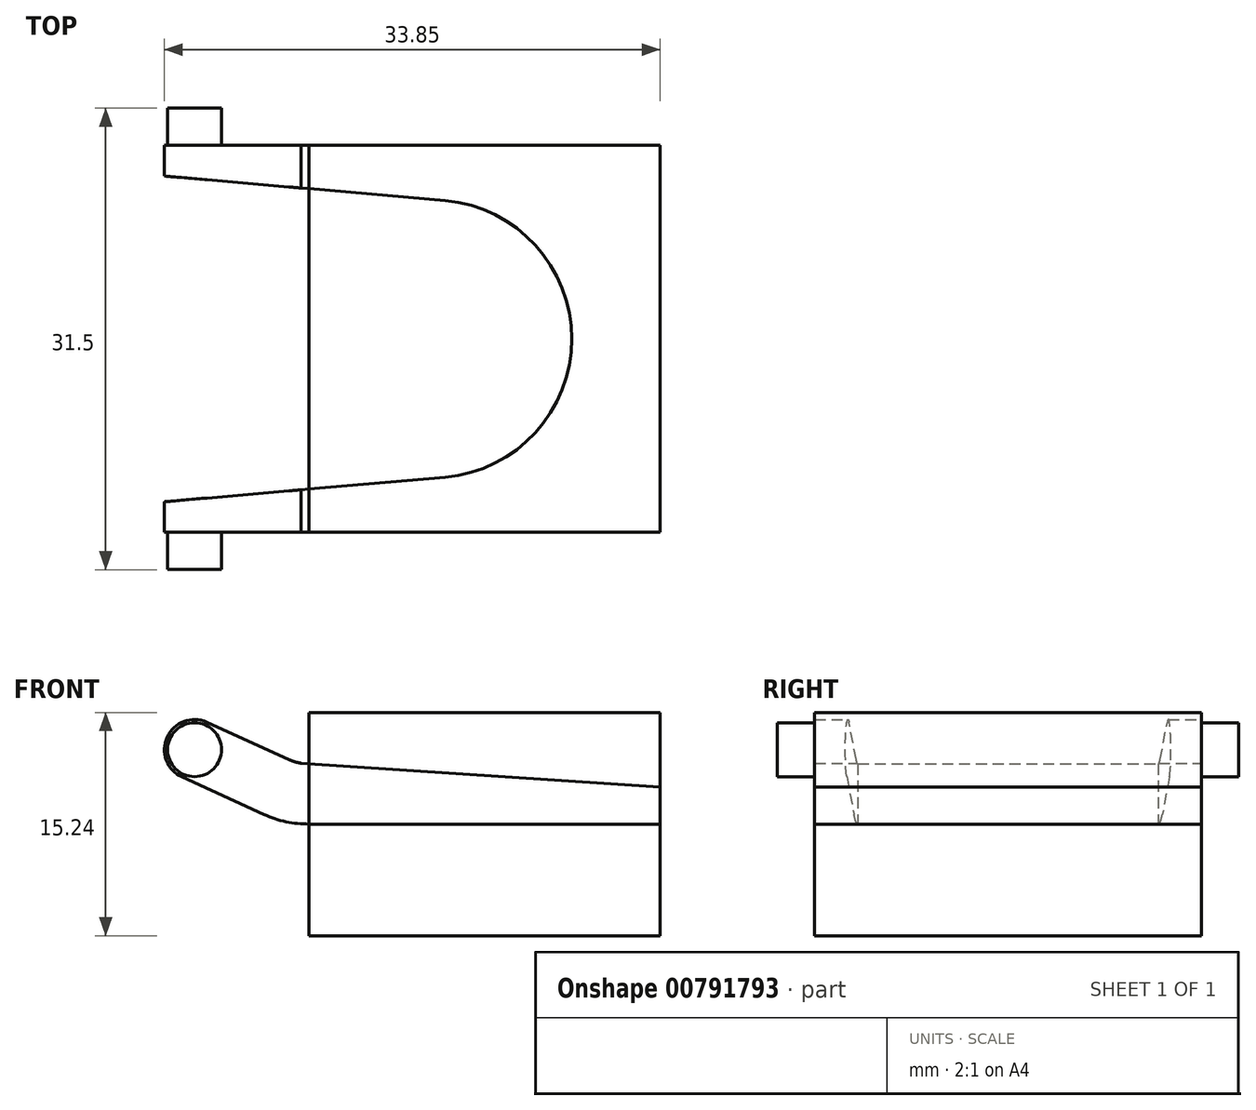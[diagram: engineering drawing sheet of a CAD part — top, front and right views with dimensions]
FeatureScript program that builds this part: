
annotation { "Feature Type Name" : "Feature", "Feature Type Description" : "" }
export const myFeature = defineFeature(function(context is Context, id is Id, definition is map)
    precondition{}
    {
        {
            var Q0;
            Q0=qCreatedBy(makeId("Front.planeOp"),FACE);
            var sketch = newSketch(context, id + "F0", { "sketchPlane" : qUnion([Q0])});
            skLineSegment(sketch, "E0", {"start": v(18.98, -6.5) * mm, "end": v(-4.99, -6.5) * mm});
            skLineSegment(sketch, "E1", {"start": v(-8.07, -5.85) * mm, "end": v(-13.66, -3.3) * mm});
            skLineSegment(sketch, "E2", {"start": v(18.98, -6.5) * mm, "end": v(18.98, -3.97) * mm});
            skLineSegment(sketch, "E3", {"start": v(18.98, -3.97) * mm, "end": v(-5.54, -2.36) * mm});
            skLineSegment(sketch, "E4", {"start": v(-11.96, 0.44) * mm, "end": v(-6.36, -2.1) * mm});
            skArc(sketch, "E5", {"start": v(-13.66, -3.3) * mm, "mid": v(-14.68, -0.57) * mm, "end": v(-11.96, 0.44) * mm});
            skLineSegment(sketch, "E6", {"start": v(-8.07, -5.85) * mm, "end": v(-6.36, -2.1) * mm, "construction": true});
            skArc(sketch, "E7", {"start": v(-8.07, -5.85) * mm, "mid": v(-6.57, -6.35) * mm, "end": v(-4.99, -6.5) * mm});
            skArc(sketch, "E8", {"start": v(-6.36, -2.1) * mm, "mid": v(-5.96, -2.26) * mm, "end": v(-5.54, -2.36) * mm});
            skSolve(sketch);
        }
        {
            var Q0;
            Q0=makeQuery(id+"F0.imprint","IMPRINT",FACE,{"disambiguationData":[TD([[makeQuery(id+"F0.imprint","IMPRINT",EDGE,{"derivedFrom":sQuery(id+"F0.wireOp",EDGE,"E0")}),-1.0]])]});
            extrude(context, id + "F1", {"entities" : qUnion([Q0]), "depth" : 26.42 * mm, "offsetDistance" : 25.4 * mm});
        }
        {
            var Q0;
            Q0=makeQuery(id+"F1.opExtrude","CAP_FACE",FACE,{"disambiguationData":[OSD([sQuery(id+"F0.wireOp",EDGE,"E0"),sQuery(id+"F0.wireOp",EDGE,"E1"),sQuery(id+"F0.wireOp",EDGE,"E2"),sQuery(id+"F0.wireOp",EDGE,"E3"),sQuery(id+"F0.wireOp",EDGE,"E4"),sQuery(id+"F0.wireOp",EDGE,"E5"),sQuery(id+"F0.wireOp",EDGE,"E7"),sQuery(id+"F0.wireOp",EDGE,"E8")])],"isStart":false});
            var sketch = newSketch(context, id + "F2", { "sketchPlane" : qUnion([Q0])});
            skArc(sketch, "E9.0", {"start": v(-13.66, -3.3) * mm, "mid": v(-14.68, -0.57) * mm, "end": v(-11.96, 0.44) * mm});
            skCircle(sketch, "E10", {"center": v(-12.8, -1.43) * mm, "radius": 1.84 * mm});
            skSolve(sketch);
        }
        {
            var Q0;
            Q0=makeQuery(id+"F2.imprint","IMPRINT",FACE,{"disambiguationData":[TD([[makeQuery(id+"F2.imprint","IMPRINT",EDGE,{"derivedFrom":sQuery(id+"F2.wireOp",EDGE,"E10")}),1.0]])]});
            extrude(context, id + "F3", {"entities" : qUnion([Q0]), "depth" : 2.54 * mm, "offsetDistance" : 25.4 * mm});
        }
        {
            var Q0;
            Q0=makeQuery(id+"F1.opExtrude","CAP_FACE",FACE,{"disambiguationData":[OSD([sQuery(id+"F0.wireOp",EDGE,"E0"),sQuery(id+"F0.wireOp",EDGE,"E1"),sQuery(id+"F0.wireOp",EDGE,"E2"),sQuery(id+"F0.wireOp",EDGE,"E3"),sQuery(id+"F0.wireOp",EDGE,"E4"),sQuery(id+"F0.wireOp",EDGE,"E5"),sQuery(id+"F0.wireOp",EDGE,"E7"),sQuery(id+"F0.wireOp",EDGE,"E8")])],"isStart":true});
            var Q1;
            Q1=makeQuery(id+"F1.opExtrude","CAP_FACE",FACE,{"disambiguationData":[OSD([sQuery(id+"F0.wireOp",EDGE,"E0"),sQuery(id+"F0.wireOp",EDGE,"E1"),sQuery(id+"F0.wireOp",EDGE,"E2"),sQuery(id+"F0.wireOp",EDGE,"E3"),sQuery(id+"F0.wireOp",EDGE,"E4"),sQuery(id+"F0.wireOp",EDGE,"E5"),sQuery(id+"F0.wireOp",EDGE,"E7"),sQuery(id+"F0.wireOp",EDGE,"E8")])],"isStart":false});
            cPlane(context, id + "F4", {"entities" : qUnion([Q0, Q1]), "cplaneType" : CPlaneType.MID_PLANE, "offset" : 25.4 * mm, "width" : 152.4 * mm, "height" : 152.4 * mm});
        }
        {
            var Q0;
            Q0=makeQuery(id+"F3.opExtrude","SWEPT_BODY",BODY,{"disambiguationData":[OSD([sQuery(id+"F2.wireOp",EDGE,"E10")])]});
            var Q1;
            Q1=qCreatedBy(id+"F4.planeOp",FACE);
            mirror(context, id + "F5", {"entities" : qUnion([Q0]), "mirrorPlane" : qUnion([Q1])});
        }
        {
            var Q0;
            Q0=makeQuery(id+"F1.opExtrude","SWEPT_FACE",FACE,{"disambiguationData":[OSD([sQuery(id+"F0.wireOp",EDGE,"E0")])]});
            var sketch = newSketch(context, id + "F6", { "sketchPlane" : qUnion([Q0])});
            skLineSegment(sketch, "E11", {"start": v(-16.56, 24.47) * mm, "end": v(-16.56, 1.94) * mm});
            skLineSegment(sketch, "E12", {"start": v(-16.56, 1.94) * mm, "end": v(4.29, 3.77) * mm});
            skLineSegment(sketch, "E13", {"start": v(-16.56, 24.47) * mm, "end": v(4.29, 22.65) * mm});
            skPoint(sketch, "E14", {"position": v(-16.56, 13.2) * mm});
            skPoint(sketch, "E15", {"position": v(-4.99, 13.2) * mm});
            skArc(sketch, "E16", {"start": v(4.29, 22.65) * mm, "mid": v(12.94, 13.2) * mm, "end": v(4.29, 3.77) * mm});
            skSolve(sketch);
        }
        {
            var Q0;
            {var subQ0=sQuery(id+"F6.wireOp",EDGE,"E11");Q0=makeQuery(id+"F6.imprint","IMPRINT",FACE,{"disambiguationData":[TD([[makeQuery(id+"F6.imprint","IMPRINT",EDGE,{"derivedFrom":subQ0}),1.0]])]});}
            var Q1;
            {var subQ0=sQuery(id+"F6.wireOp",EDGE,"E16");Q1=makeQuery(id+"F6.imprint","IMPRINT",FACE,{"disambiguationData":[TD([[makeQuery(id+"F6.imprint","IMPRINT",EDGE,{"derivedFrom":subQ0}),-1.0]])]});}
            extrude(context, id + "F7", {"entities" : qUnion([Q0, Q1]), "oppositeDirection" : true, "depth" : 15.24 * mm, "offsetDistance" : 25.4 * mm, "symmetric" : true});
        }
        {
            var Q0;
            Q0=makeQuery(id+"F7.opExtrude","SWEPT_BODY",BODY,{"disambiguationData":[OSD([sQuery(id+"F6.wireOp",EDGE,"E11"),sQuery(id+"F6.wireOp",EDGE,"E12"),sQuery(id+"F6.wireOp",EDGE,"E13"),sQuery(id+"F6.wireOp",EDGE,"E16")])]});
            var Q1;
            Q1=makeQuery(id+"F1.opExtrude","SWEPT_BODY",BODY,{"disambiguationData":[OSD([sQuery(id+"F0.wireOp",EDGE,"E0"),sQuery(id+"F0.wireOp",EDGE,"E1"),sQuery(id+"F0.wireOp",EDGE,"E2"),sQuery(id+"F0.wireOp",EDGE,"E3"),sQuery(id+"F0.wireOp",EDGE,"E4"),sQuery(id+"F0.wireOp",EDGE,"E5"),sQuery(id+"F0.wireOp",EDGE,"E7"),sQuery(id+"F0.wireOp",EDGE,"E8")])]});
            booleanBodies(context, id + "F8", {"operationType" : BooleanOperationType.SUBTRACTION, "tools" : qUnion([Q0]), "targets" : qUnion([Q1])});
        }
    });
